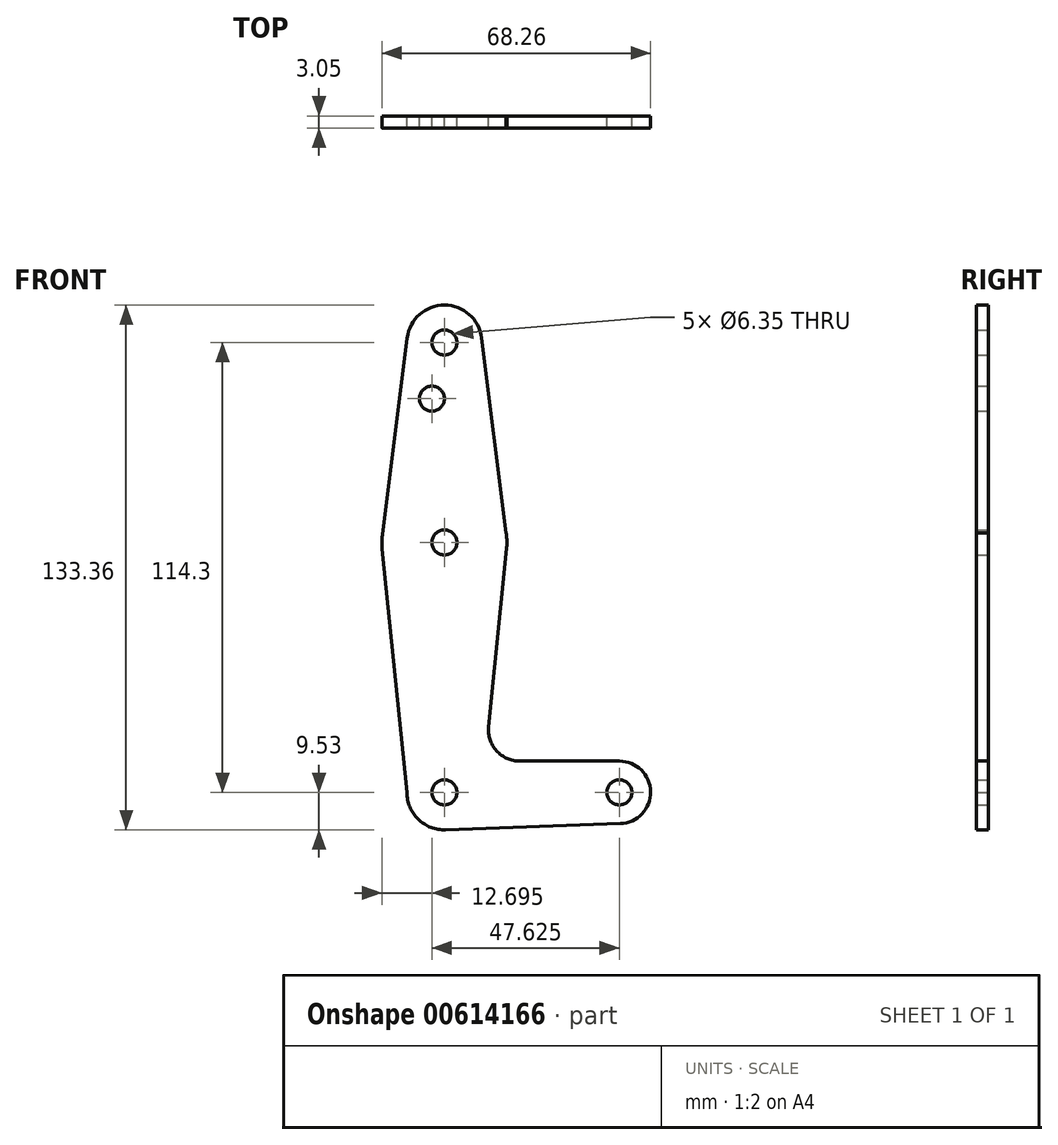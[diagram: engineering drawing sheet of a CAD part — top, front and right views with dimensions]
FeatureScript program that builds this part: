
annotation { "Feature Type Name" : "Feature", "Feature Type Description" : "" }
export const myFeature = defineFeature(function(context is Context, id is Id, definition is map)
    precondition{}
    {
        {
            var Q0;
            Q0=qCreatedBy(makeId("Front.planeOp"),FACE);
            var sketch = newSketch(context, id + "F0", { "sketchPlane" : qUnion([Q0])});
            skLineSegment(sketch, "E0", {"start": v(44.45, 0) * mm, "end": v(0, 0) * mm});
            skLineSegment(sketch, "E1", {"start": v(0, 0) * mm, "end": v(0, 114.3) * mm});
            skCircle(sketch, "E2", {"center": v(0, 0) * mm, "radius": 9.53 * mm});
            skCircle(sketch, "E3", {"center": v(44.45, 0) * mm, "radius": 7.94 * mm});
            skCircle(sketch, "E4", {"center": v(0, 114.3) * mm, "radius": 9.53 * mm});
            skCircle(sketch, "E5", {"center": v(0, 63.5) * mm, "radius": 15.88 * mm});
            skLineSegment(sketch, "E6", {"start": v(-9.45, 115.5) * mm, "end": v(-15.75, 65.48) * mm});
            skLineSegment(sketch, "E7", {"start": v(9.45, 115.49) * mm, "end": v(15.8, 65.09) * mm});
            skLineSegment(sketch, "E8", {"start": v(15.8, 61.91) * mm, "end": v(11.25, 16.68) * mm});
            skLineSegment(sketch, "E9", {"start": v(19.16, 7.94) * mm, "end": v(44.45, 7.94) * mm});
            skLineSegment(sketch, "E10", {"start": v(0, -9.53) * mm, "end": v(44.73, -7.93) * mm});
            skCircle(sketch, "E11", {"center": v(0, 114.3) * mm, "radius": 3.18 * mm});
            skCircle(sketch, "E12", {"center": v(0, 63.5) * mm, "radius": 3.18 * mm});
            skCircle(sketch, "E13", {"center": v(0, 0) * mm, "radius": 3.18 * mm});
            skCircle(sketch, "E14", {"center": v(44.45, 0) * mm, "radius": 3.18 * mm});
            skCircle(sketch, "E15", {"center": v(-3.18, 100.03) * mm, "radius": 3.18 * mm});
            skArc(sketch, "E16.filletArc", {"start": v(11.25, 16.68) * mm, "mid": v(13.26, 10.55) * mm, "end": v(19.16, 7.94) * mm});
            skLineSegment(sketch, "E17", {"start": v(-9.52, 0) * mm, "end": v(-15.8, 61.9) * mm});
            skSolve(sketch);
        }
        {
            var Q0;
            Q0 = qSketchRegion(id + "F0", true);
            var Q1;
            {var subQ0=sQuery(id+"F0.wireOp",EDGE,"E2");var subQ1=sQuery(id+"F0.wireOp",EDGE,"E0");var subQ2=makeQuery(id+"F0.imprint","INTERSECT",VERTEX,{"derivedFrom":[subQ1,subQ0]});Q1=makeQuery(id+"F0.imprint","IMPRINT",FACE,{"disambiguationData":[TD([[makeQuery(id+"F0.imprint","IMPRINT",EDGE,{"disambiguationData":[TD([[subQ2,-1.0]])],"derivedFrom":subQ1}),-1.0]])]});}
            extrude(context, id + "F1", {"entities" : qUnion([Q0, Q1]), "depth" : 3.05 * mm, "offsetDistance" : 25.4 * mm});
        }
    });
